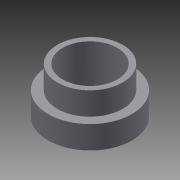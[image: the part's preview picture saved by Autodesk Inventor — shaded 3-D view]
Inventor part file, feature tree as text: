
AUTODESK INVENTOR PART (.ipt)
format: ipt  version: 2015 (Build 190159000, 159)  size: 89,600 bytes
history: native  units: in
note: dims shown in document units (in); Inventor stores cm internally (conversion verified against a paired STEP export)
features: extrude x2, sketch x2
ambient origin geometry x8: Origin, YZ Plane, XZ Plane, XY Plane, X Axis, Y Axis, Z Axis, Center Point
bodies: Solid1 (feature_tree)
feature tree (4):
  extrude  "Extrusion1"  Depth=0.275in
  extrude  "Extrusion2"  Depth=0.075in
  sketch  "Sketch1"  dims[d0=0.18in d1=0.275in]
  sketch  "Sketch2"  dims[d2=0.075in d3=0.0in d4=0.215in d5=0.075in d6=0.0in]
